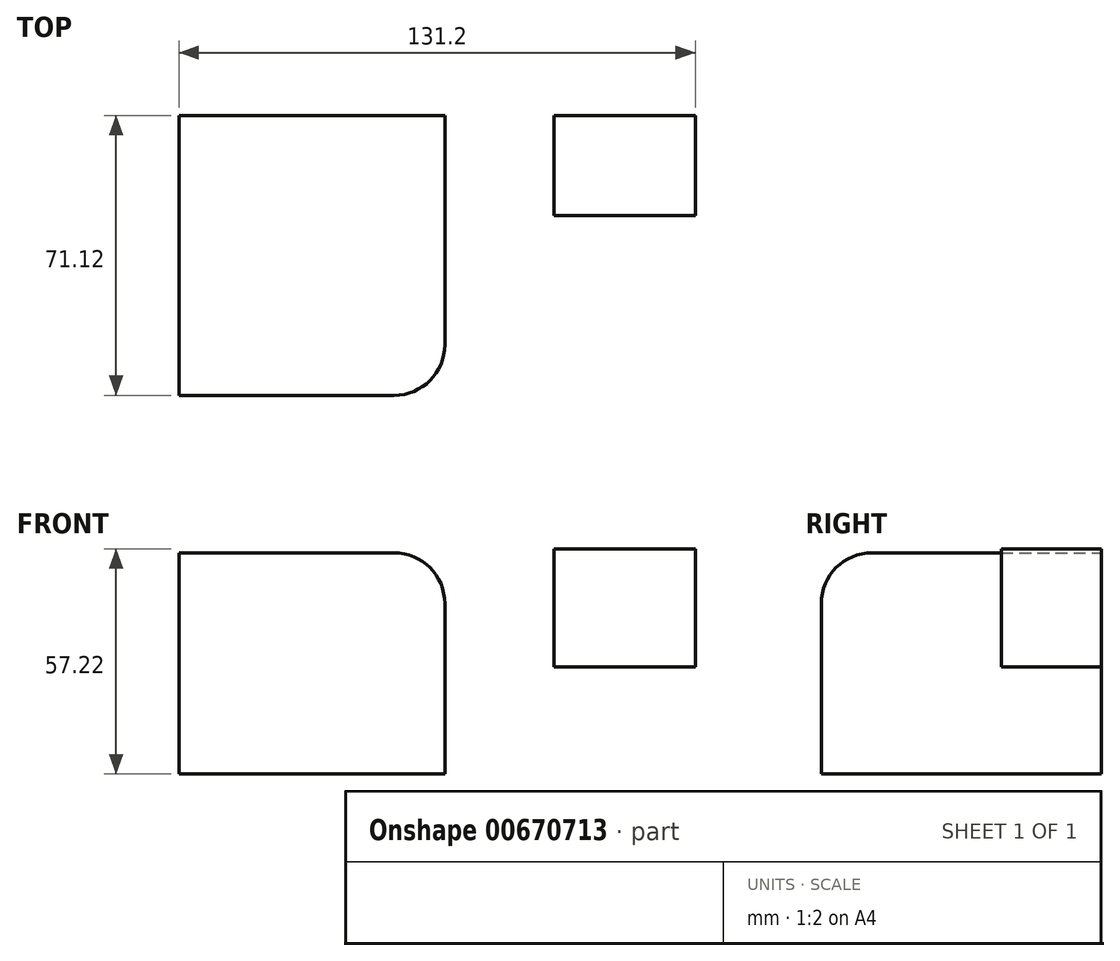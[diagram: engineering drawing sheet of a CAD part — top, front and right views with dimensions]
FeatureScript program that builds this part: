
annotation { "Feature Type Name" : "Feature", "Feature Type Description" : "" }
export const myFeature = defineFeature(function(context is Context, id is Id, definition is map)
    precondition{}
    {
        {
            var Q0;
            Q0=qCreatedBy(makeId("Front.planeOp"),FACE);
            var sketch = newSketch(context, id + "F0", { "sketchPlane" : qUnion([Q0])});
            skLineSegment(sketch, "E0.bottom", {"start": v(-67.54, 36.45) * mm, "end": v(0, 36.45) * mm});
            skLineSegment(sketch, "E0.top", {"start": v(-67.54, -19.78) * mm, "end": v(0, -19.78) * mm});
            skLineSegment(sketch, "E0.left", {"start": v(-67.54, 36.45) * mm, "end": v(-67.54, -19.78) * mm});
            skLineSegment(sketch, "E0.right", {"start": v(0, 36.45) * mm, "end": v(0, -19.78) * mm});
            skSolve(sketch);
        }
        {
            var Q0;
            Q0=makeQuery(id+"F0.imprint","IMPRINT",FACE,{"disambiguationData":[TD([[makeQuery(id+"F0.imprint","IMPRINT",EDGE,{"derivedFrom":sQuery(id+"F0.wireOp",EDGE,"E0.bottom")}),-1.0]])]});
            extrude(context, id + "F1", {"entities" : qUnion([Q0]), "depth" : 71.12 * mm, "offsetDistance" : 25.4 * mm});
        }
        {
            var Q0;
            Q0=makeQuery(id+"F1.opExtrude","CAP_EDGE",EDGE,{"disambiguationData":[OSD([sQuery(id+"F0.wireOp",EDGE,"E0.bottom")])],"isStart":false});
            var Q1;
            Q1=makeQuery(id+"F1.opExtrude","SWEPT_EDGE",EDGE,{"disambiguationData":[OSD([sQuery(id+"F0.wireOp",EDGE,"E0.bottom"),sQuery(id+"F0.wireOp",EDGE,"E0.right")])]});
            var Q2;
            Q2=makeQuery(id+"F1.opExtrude","CAP_EDGE",EDGE,{"disambiguationData":[OSD([sQuery(id+"F0.wireOp",EDGE,"E0.right")])],"isStart":false});
            fillet(context, id + "F2", {"entities" : qUnion([Q0, Q1, Q2]), "radius" : 12.88 * mm, "tangentPropagation" : true, "allowEdgeOverflow" : false});
        }
        {
            var Q0;
            Q0=qCreatedBy(makeId("Front.planeOp"),FACE);
            var sketch = newSketch(context, id + "F3", { "sketchPlane" : qUnion([Q0])});
            skLineSegment(sketch, "E1.bottom", {"start": v(27.77, 37.44) * mm, "end": v(63.66, 37.44) * mm});
            skLineSegment(sketch, "E1.top", {"start": v(27.77, 7.45) * mm, "end": v(63.66, 7.45) * mm});
            skLineSegment(sketch, "E1.left", {"start": v(27.77, 37.44) * mm, "end": v(27.77, 7.45) * mm});
            skLineSegment(sketch, "E1.right", {"start": v(63.66, 37.44) * mm, "end": v(63.66, 7.45) * mm});
            skSolve(sketch);
        }
        {
            var Q0;
            Q0=makeQuery(id+"F3.imprint","IMPRINT",FACE,{"disambiguationData":[TD([[makeQuery(id+"F3.imprint","IMPRINT",EDGE,{"derivedFrom":sQuery(id+"F3.wireOp",EDGE,"E1.bottom")}),-1.0]])]});
            extrude(context, id + "F4", {"entities" : qUnion([Q0]), "depth" : 25.4 * mm, "offsetDistance" : 25.4 * mm});
        }
    });
